# Revit family: QF_EVEREST_ESWQ2D2
name_source: partatom
category: Specialty Equipment
revit_build: Autodesk Revit 2015 (Build: 20141119_0715(x64)
units: mm (PartAtom-declared; Revit-internal decimal feet)

## types (1)
- ESWQ2D2
    Apparent Power = 0 VA
    BTUH = 4237.0 Btu/h
    Conn Conduit = Yes
    Conn Plug = NEMA 5-15P
    Cycle = 60 Hz
    Depth = 803 mm
    Description = DOOR & DRAWER COMBO UPRIGHT REACH–IN FREEZER
    Elec Conn Connection Height = 0 mm  [stored 0 ft]
    Elec Conn RI Height = 0 mm  [stored 0 ft]
    Electrical Remarks = HAS (X1) 1/4+ HP COMPRESSOR FOR REF SIDE AND (X1) 1/3 HP COMPRESSOR FOR FRZ SIDE. BTUH IS CALCULATED FOR (2) COMPRESSORS. EACH COMPRESSOR COMES WITH R290 REFRIGERANT.
    FL Amps = 6 A
    Foodservice Equipment Identifier = Yes
    HP = 1/4+ (R) 1/3 (F)
    Height = 2010 mm  [stored 6.59449 ft]
    Identify Quantity as Lot = Yes
    Length = 1500 mm  [stored 4.92126 ft]
    Manufacturer = EVEREST
    Max Overcurrent Protection = 0 A
    Min Ckt Ampacity = 0 A
    Model = ESWQ2D2
    Number of Poles = 1
    Phase = 1
    Refrigerant Type = R290
    Refrigerant Volume = 0.00 kip
    Volts = 115 V
    Watts = 633 W
    Weight in Pounds = 556

note: [stored X ft] marks values corroborated as IEEE doubles in the binary element streams (Revit-internal decimal feet)

## geometry (parser evidence)
native form markers: Sweep x6
no freeform markers — native parametric forms only
